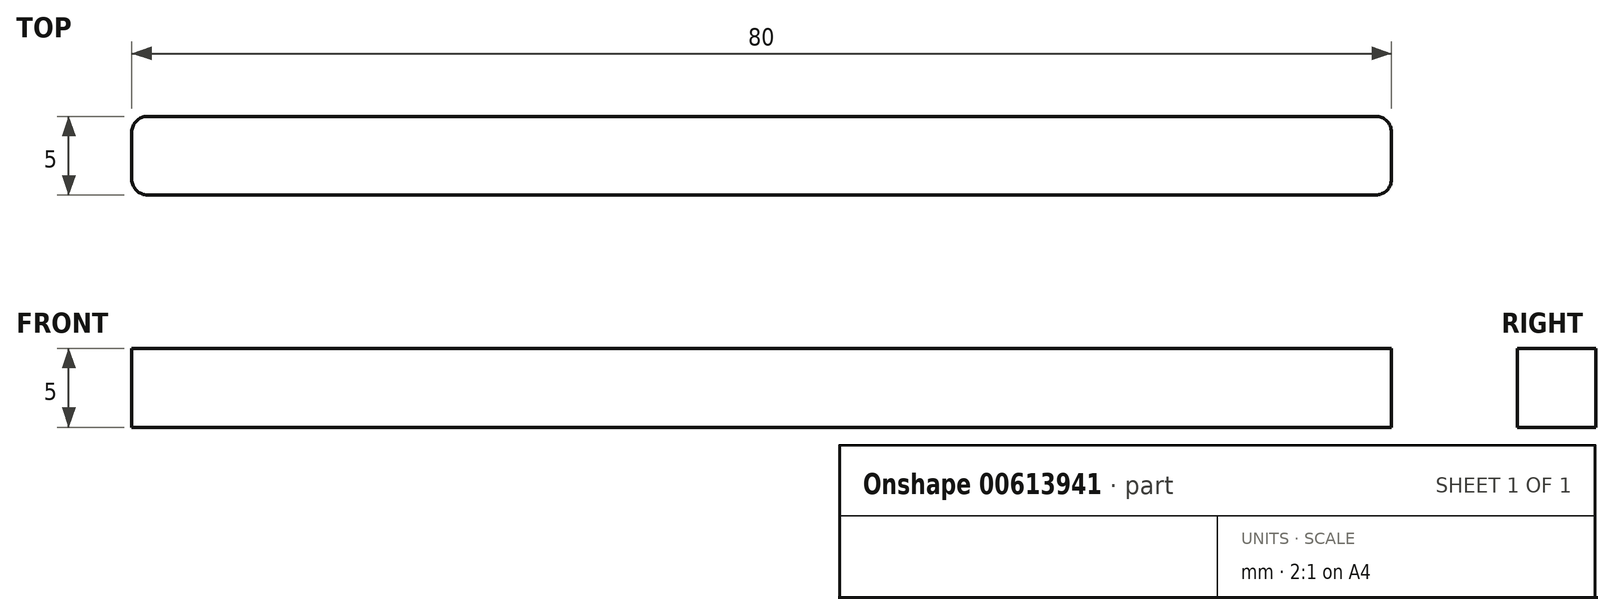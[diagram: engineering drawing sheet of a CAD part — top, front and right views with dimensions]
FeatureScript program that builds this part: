
annotation { "Feature Type Name" : "Feature", "Feature Type Description" : "" }
export const myFeature = defineFeature(function(context is Context, id is Id, definition is map)
    precondition{}
    {
        {
            var Q0;
            Q0=qCreatedBy(makeId("Top.planeOp"),FACE);
            var sketch = newSketch(context, id + "F0", { "sketchPlane" : qUnion([Q0])});
            skLineSegment(sketch, "E0.bottom", {"start": v(-39, -2.5) * mm, "end": v(39, -2.5) * mm});
            skLineSegment(sketch, "E0.top", {"start": v(-39, 2.5) * mm, "end": v(39, 2.5) * mm});
            skLineSegment(sketch, "E0.left", {"start": v(-40, -1.5) * mm, "end": v(-40, 1.5) * mm});
            skLineSegment(sketch, "E0.right", {"start": v(40, -1.5) * mm, "end": v(40, 1.5) * mm});
            skPoint(sketch, "E1.visualSharp", {"position": v(-40, 2.5) * mm});
            skArc(sketch, "E1.filletArc", {"start": v(-39, 2.5) * mm, "mid": v(-39.7, 2.2) * mm, "end": v(-40, 1.5) * mm});
            skPoint(sketch, "E2.visualSharp", {"position": v(-40, -2.5) * mm});
            skArc(sketch, "E2.filletArc", {"start": v(-40, -1.5) * mm, "mid": v(-39.7, -2.2) * mm, "end": v(-39, -2.5) * mm});
            skPoint(sketch, "E3.visualSharp", {"position": v(40, 2.5) * mm});
            skArc(sketch, "E3.filletArc", {"start": v(40, 1.5) * mm, "mid": v(39.7, 2.2) * mm, "end": v(39, 2.5) * mm});
            skPoint(sketch, "E4.visualSharp", {"position": v(40, -2.5) * mm});
            skArc(sketch, "E4.filletArc", {"start": v(39, -2.5) * mm, "mid": v(39.7, -2.2) * mm, "end": v(40, -1.5) * mm});
            skSolve(sketch);
        }
        {
            var Q0;
            Q0 = qSketchRegion(id + "F0", true);
            extrude(context, id + "F1", {"entities" : qUnion([Q0]), "depth" : 5 * mm, "offsetDistance" : 25 * mm});
        }
    });
